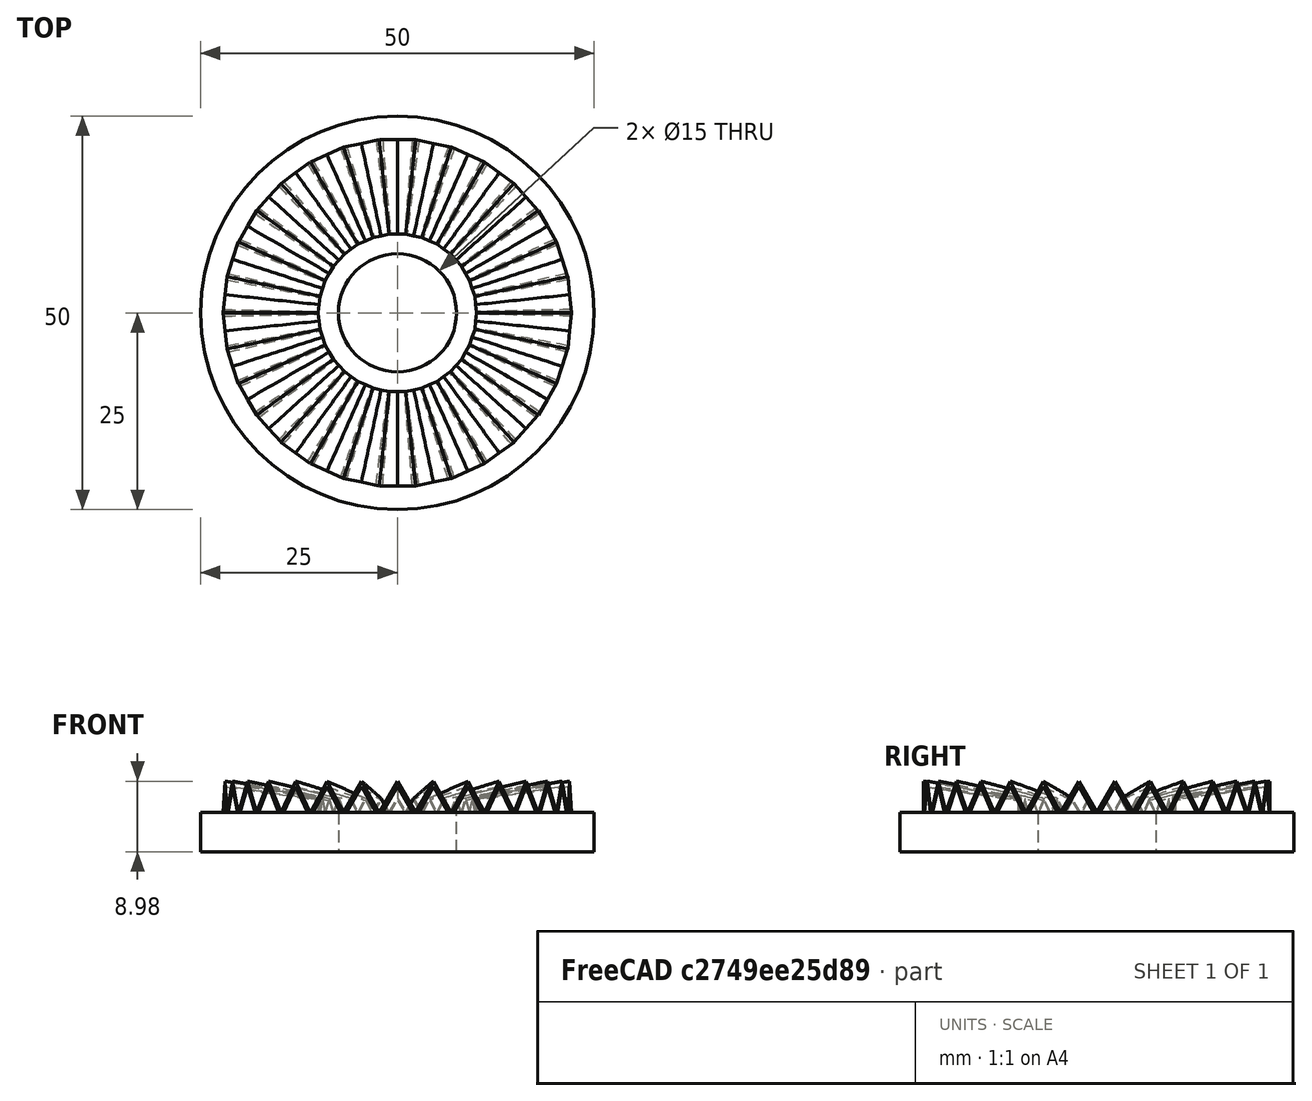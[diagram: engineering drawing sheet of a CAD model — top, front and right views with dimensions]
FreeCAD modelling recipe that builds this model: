
FCSTD DOCUMENT  (FreeCAD 1.1R20251125 (Git shallow))
Label: 20260120
License: All rights reserved
LicenseURL: http://en.wikipedia.org/wiki/All_rights_reserved
objects: Sketcher::SketchObject×8, App::Point×2, PartDesign::Pad×2, PartDesign::AdditiveLoft×2, PartDesign::PolarPattern×2, PartDesign::Body×2, Measure::MeasureDistance×2, App::DocumentObjectGroup×1, App::LinkGroup×1, App::Link×1
note: 34 computed .brp shape members not serialized (recipe doc carries the construction recipe); baked Part::Feature solids carry a one-line shape summary decoded from their .brp

FEATURE [App::Point] Origin001
  Role = Origin
FEATURE [Sketcher::SketchObject] Sketch
  ArcFitTolerance = 1e-06
  AttachmentSupport = -> [Origin]
  ExternalTypes = [0]
  FullyConstrained = true
  MakeInternals = false
  MapMode = 5
  sketch-geometry (2):
    g0: Circle CenterX=0 CenterY=0 CenterZ=0 NormalX=0 NormalY=0 NormalZ=1 AngleXU=0 Radius=25
    g1: Circle CenterX=0 CenterY=0 CenterZ=0 NormalX=0 NormalY=0 NormalZ=1 AngleXU=0 Radius=7.5
  constraints (4):
    c: Diameter(g0) = 50
    c: Coincident(g0,g-1)
    c: Diameter(g1) = 15
    c: Coincident(g0,g1)
FEATURE [PartDesign::Pad] Pad
  Direction = (0,0,1)
  Length = 5
  Length2 = 10
  Profile = -> Sketch
  ReferenceAxis = -> Sketch [N_Axis]
  Refine = true
  SideType = 0
  Suppressed = false
  Type = 0
  Type2 = 0
FEATURE [Sketcher::SketchObject] Sketch001
  ArcFitTolerance = 1e-06
  AttachmentSupport = -> [Pad]
  ExternalTypes = [0]
  FullyConstrained = true
  MakeInternals = false
  MapMode = 5
  Placement = pos=(0,0,5) rot=(0,0,1;0rad)
  sketch-geometry (6):
    g0: ArcOfCircle [constr] CenterX=0 CenterY=0 CenterZ=0 NormalX=0 NormalY=0 NormalZ=1 AngleXU=0 Radius=10 StartAngle=1.46608 EndAngle=1.67552
    g1: ArcOfCircle [constr] CenterX=0 CenterY=0 CenterZ=0 NormalX=0 NormalY=0 NormalZ=1 AngleXU=0 Radius=22 StartAngle=1.46608 EndAngle=1.67552
    g2: LineSegment [constr] StartX=0 StartY=0 StartZ=0 EndX=1.04528 EndY=9.94522 EndZ=0
    g3: LineSegment [constr] StartX=0 StartY=0 StartZ=0 EndX=-1.04528 EndY=9.94522 EndZ=0
    g4: LineSegment StartX=-1.04528 StartY=9.94522 StartZ=0 EndX=-2.29963 EndY=21.8795 EndZ=0
    g5: LineSegment StartX=2.29963 StartY=21.8795 StartZ=0 EndX=1.04528 EndY=9.94522 EndZ=0
  constraints (16):
    c: Coincident(g0,g-1)
    c: Coincident(g1,g0)
    c: Coincident(g2,g0)
    c: Coincident(g2,g0)
    c: Coincident(g3,g0)
    c: Coincident(g3,g0)
    c: Coincident(g3,g4)
    c: Coincident(g4,g1)
    c: Parallel(g4,g3)
    c: Symmetric(g1,g1,g-2)
    c: Radius(g1) = 22
    c: Radius(g0) = 10
    c: Coincident(g5,g1)
    c: Coincident(g5,g0)
    c: Parallel(g5,g2)
    c: Angle(g5,g4) = 0.20944
FEATURE [Sketcher::SketchObject] Sketch002
  ArcFitTolerance = 1e-06
  AttachmentOffset = pos=(0,0,-10) rot=(0,0,1;0rad)
  AttachmentSupport = -> [Origin]
  ExternalTypes = [0]
  FullyConstrained = true
  MakeInternals = false
  MapMode = 5
  Placement = pos=(0,10,-2.2e-15) rot=(1,0,0;1.5708rad)
  expr: Constraints[10] = href(Body.BackTooth)
  sketch-geometry (4):
    g0: LineSegment StartX=1.0455 StartY=5 StartZ=0 EndX=4e-16 EndY=6.81086 EndZ=0
    g1: LineSegment StartX=4e-16 StartY=6.81086 StartZ=0 EndX=-1.0455 EndY=5 EndZ=0
    g2: LineSegment StartX=-1.0455 StartY=5 StartZ=0 EndX=1.0455 EndY=5 EndZ=0
    g3: Circle [constr] CenterX=0 CenterY=5.60362 CenterZ=0 NormalX=0 NormalY=0 NormalZ=1 AngleXU=0 Radius=1.20724
  constraints (12):
    c: Coincident(g0,g1)
    c: Coincident(g1,g2)
    c: Coincident(g2,g0)
    c: Equal(g0,g1)
    c: Equal(g0,g2)
    c: PointOnObject(g0,g3)
    c: PointOnObject(g1,g3)
    c: PointOnObject(g2,g3)
    c: PointOnObject(g3,g-2)
    c: Horizontal(g2)
    c: Distance(g2,g2) = 2.091
    c: DistanceY(g-1,g0) = 5
FEATURE [Sketcher::SketchObject] Sketch003
  ArcFitTolerance = 1e-06
  AttachmentOffset = pos=(0,0,-22) rot=(0,0,1;0rad)
  AttachmentSupport = -> [Origin]
  ExternalTypes = [0]
  FullyConstrained = true
  MakeInternals = false
  MapMode = 5
  Placement = pos=(0,22,-4.9e-15) rot=(1,0,0;1.5708rad)
  expr: Constraints[10] = href(Body.FrontTooth)
  sketch-geometry (4):
    g0: LineSegment StartX=0 StartY=8.98285 StartZ=0 EndX=-2.2995 EndY=5 EndZ=0
    g1: LineSegment StartX=-2.2995 StartY=5 StartZ=0 EndX=2.2995 EndY=5 EndZ=0
    g2: LineSegment StartX=2.2995 StartY=5 StartZ=0 EndX=0 EndY=8.98285 EndZ=0
    g3: Circle [constr] CenterX=0 CenterY=6.32762 CenterZ=0 NormalX=0 NormalY=0 NormalZ=1 AngleXU=0 Radius=2.65523
  constraints (12):
    c: Coincident(g0,g1)
    c: Coincident(g1,g2)
    c: Coincident(g2,g0)
    c: Equal(g0,g1)
    c: Equal(g0,g2)
    c: PointOnObject(g0,g3)
    c: PointOnObject(g1,g3)
    c: PointOnObject(g2,g3)
    c: PointOnObject(g3,g-2)
    c: PointOnObject(g2,g-2)
    c: Distance(g1,g1) = 4.599
    c: DistanceY(g-1,g1) = 5
FEATURE [PartDesign::AdditiveLoft] AdditiveLoft
  BaseFeature = -> Pad
  Closed = false
  Profile = -> Sketch003
  Refine = true
  Ruled = false
  Sections = -> [Sketch002]
  Suppressed = false
FEATURE [PartDesign::PolarPattern] PolarPattern
  Angle = 360
  Axis = -> Z_Axis
  BaseFeature = -> AdditiveLoft
  Mode = 0
  Occurrences = 30
  Offset = 120
  Originals = -> [AdditiveLoft]
  Refine = true
  SpacingPattern = [0]
  Spacings = [-1,-1,-1,-1,-1,-1,-1,-1,-1,-1,-1,-1,-1,-1,-1,-1,-1,-1,-1,-1,-1,-1,-1,-1,-1,-1,-1,-1,-1]
  Suppressed = false
  TransformMode = 0
FEATURE [PartDesign::Body] Body
  AllowCompound = true
  BackTooth = 2.091
  FrontTooth = 4.599
  Group = -> [Sketch,Pad,Sketch001,Sketch002,Sketch003,AdditiveLoft,PolarPattern]
  Origin = -> Origin
  Tip = -> PolarPattern
FEATURE [Measure::MeasureDistance] Distance  label="Distance: 2,091 mm"
  Distance = 2.09057
  DistanceX = 2.09057
  DistanceY = 0
  DistanceZ = 0
  Element1 = -> Body [Sketch001.Vertex1]
  Element2 = -> Body [Sketch001.Vertex4]
  Position1 = (-1.04528,9.94522,5)
  Position2 = (1.04528,9.94522,5)
FEATURE [Measure::MeasureDistance] Distance001  label="Distance001: 4,599 mm"
  Distance = 4.59925
  DistanceX = 4.59925
  DistanceY = 0
  DistanceZ = 0
  Element1 = -> Body [Sketch001.Vertex2]
  Element2 = -> Body [Sketch001.Vertex3]
  Position1 = (-2.29963,21.8795,5)
  Position2 = (2.29963,21.8795,5)
FEATURE [App::DocumentObjectGroup] Measurements
  Group = -> [Distance,Distance001]
FEATURE [App::Point] Origin002
  Role = Origin
FEATURE [Sketcher::SketchObject] Sketch004
  ArcFitTolerance = 1e-06
  AttachmentOffset = pos=(0,0,-10) rot=(0,0,1;0rad)
  AttachmentSupport = -> [Origin003]
  ExternalTypes = [0]
  FullyConstrained = true
  MakeInternals = false
  MapMode = 5
  Placement = pos=(0,10,-2.2e-15) rot=(1,0,0;1.5708rad)
  expr: Constraints[10] = href(Body001.BackTooth)
  sketch-geometry (4):
    g0: LineSegment StartX=0.8955 StartY=5 StartZ=0 EndX=0 EndY=6.55105 EndZ=0
    g1: LineSegment StartX=0 StartY=6.55105 StartZ=0 EndX=-0.8955 EndY=5 EndZ=0
    g2: LineSegment StartX=-0.8955 StartY=5 StartZ=0 EndX=0.8955 EndY=5 EndZ=0
    g3: Circle [constr] CenterX=0 CenterY=5.51702 CenterZ=0 NormalX=0 NormalY=0 NormalZ=1 AngleXU=0 Radius=1.03403
  constraints (12):
    c: Coincident(g0,g1)
    c: Coincident(g1,g2)
    c: Coincident(g2,g0)
    c: Equal(g0,g1)
    c: Equal(g0,g2)
    c: PointOnObject(g0,g3)
    c: PointOnObject(g1,g3)
    c: PointOnObject(g2,g3)
    c: PointOnObject(g3,g-2)
    c: Horizontal(g2)
    c: Distance(g2,g2) = 1.791
    c: DistanceY(g-1,g0) = 5
FEATURE [Sketcher::SketchObject] Sketch005
  ArcFitTolerance = 1e-06
  AttachmentOffset = pos=(0,0,-22) rot=(0,0,1;0rad)
  AttachmentSupport = -> [Origin003]
  ExternalTypes = [0]
  FullyConstrained = true
  MakeInternals = false
  MapMode = 5
  Placement = pos=(0,22,-4.9e-15) rot=(1,0,0;1.5708rad)
  expr: Constraints[10] = href(Body001.FrontTooth)
  sketch-geometry (4):
    g0: LineSegment StartX=0 StartY=8.29003 StartZ=0 EndX=-1.8995 EndY=5 EndZ=0
    g1: LineSegment StartX=-1.8995 StartY=5 StartZ=0 EndX=1.8995 EndY=5 EndZ=0
    g2: LineSegment StartX=1.8995 StartY=5 StartZ=0 EndX=0 EndY=8.29003 EndZ=0
    g3: Circle [constr] CenterX=0 CenterY=6.09668 CenterZ=0 NormalX=0 NormalY=0 NormalZ=1 AngleXU=0 Radius=2.19335
  constraints (12):
    c: Coincident(g0,g1)
    c: Coincident(g1,g2)
    c: Coincident(g2,g0)
    c: Equal(g0,g1)
    c: Equal(g0,g2)
    c: PointOnObject(g0,g3)
    c: PointOnObject(g1,g3)
    c: PointOnObject(g2,g3)
    c: PointOnObject(g3,g-2)
    c: PointOnObject(g2,g-2)
    c: Distance(g1,g1) = 3.799
    c: DistanceY(g-1,g1) = 5
FEATURE [Sketcher::SketchObject] Sketch006
  ArcFitTolerance = 1e-06
  AttachmentSupport = -> [Origin003]
  ExternalTypes = [0]
  FullyConstrained = true
  MakeInternals = false
  MapMode = 5
  sketch-geometry (2):
    g0: Circle CenterX=0 CenterY=0 CenterZ=0 NormalX=0 NormalY=0 NormalZ=1 AngleXU=0 Radius=25
    g1: Circle CenterX=0 CenterY=0 CenterZ=0 NormalX=0 NormalY=0 NormalZ=1 AngleXU=0 Radius=7.5
  constraints (4):
    c: Diameter(g0) = 50
    c: Coincident(g0,g-1)
    c: Diameter(g1) = 15
    c: Coincident(g0,g1)
FEATURE [PartDesign::Pad] Pad001
  Direction = (0,0,1)
  Length = 5
  Length2 = 10
  Profile = -> Sketch006
  ReferenceAxis = -> Sketch006 [N_Axis]
  Refine = true
  SideType = 0
  Suppressed = false
  Type = 0
  Type2 = 0
FEATURE [PartDesign::AdditiveLoft] AdditiveLoft001
  BaseFeature = -> Pad001
  Closed = false
  Profile = -> Sketch005
  Refine = true
  Ruled = false
  Sections = -> [Sketch004]
  Suppressed = false
FEATURE [PartDesign::PolarPattern] PolarPattern001
  Angle = 360
  Axis = -> Z_Axis001
  BaseFeature = -> AdditiveLoft001
  Mode = 0
  Occurrences = 30
  Offset = 120
  Originals = -> [AdditiveLoft001]
  Refine = true
  SpacingPattern = [0]
  Spacings = [-1,-1,-1,-1,-1,-1,-1,-1,-1,-1,-1,-1,-1,-1,-1,-1,-1,-1,-1,-1,-1,-1,-1,-1,-1,-1,-1,-1,-1]
  Suppressed = false
  TransformMode = 0
FEATURE [Sketcher::SketchObject] Sketch007
  ArcFitTolerance = 1e-06
  AttachmentSupport = -> [Pad001]
  ExternalTypes = [0]
  FullyConstrained = true
  MakeInternals = false
  MapMode = 5
  Placement = pos=(0,0,5) rot=(0,0,1;0rad)
  sketch-geometry (6):
    g0: ArcOfCircle [constr] CenterX=0 CenterY=0 CenterZ=0 NormalX=0 NormalY=0 NormalZ=1 AngleXU=0 Radius=10 StartAngle=1.46608 EndAngle=1.67552
    g1: ArcOfCircle [constr] CenterX=0 CenterY=0 CenterZ=0 NormalX=0 NormalY=0 NormalZ=1 AngleXU=0 Radius=22 StartAngle=1.46608 EndAngle=1.67552
    g2: LineSegment [constr] StartX=0 StartY=0 StartZ=0 EndX=1.04528 EndY=9.94522 EndZ=0
    g3: LineSegment [constr] StartX=0 StartY=0 StartZ=0 EndX=-1.04528 EndY=9.94522 EndZ=0
    g4: LineSegment StartX=-1.04528 StartY=9.94522 StartZ=0 EndX=-2.29963 EndY=21.8795 EndZ=0
    g5: LineSegment StartX=2.29963 StartY=21.8795 StartZ=0 EndX=1.04528 EndY=9.94522 EndZ=0
  constraints (16):
    c: Coincident(g0,g-1)
    c: Coincident(g1,g0)
    c: Coincident(g2,g0)
    c: Coincident(g2,g0)
    c: Coincident(g3,g0)
    c: Coincident(g3,g0)
    c: Coincident(g3,g4)
    c: Coincident(g4,g1)
    c: Parallel(g4,g3)
    c: Symmetric(g1,g1,g-2)
    c: Radius(g1) = 22
    c: Radius(g0) = 10
    c: Coincident(g5,g1)
    c: Coincident(g5,g0)
    c: Parallel(g5,g2)
    c: Angle(g5,g4) = 0.20944
FEATURE [PartDesign::Body] Body001  label="Body002"
  AllowCompound = true
  BackTooth = 1.791
  FrontTooth = 3.799
  Group = -> [Sketch006,Pad001,Sketch007,Sketch004,Sketch005,AdditiveLoft001,PolarPattern001]
  Origin = -> Origin003
  Tip = -> PolarPattern001
FEATURE [App::LinkGroup] CopyOnChangeGroup
  ElementList = -> [Body001,Sketch007,PolarPattern001,AdditiveLoft001,Pad001,Sketch006,Sketch005,Sketch004,Origin003,Origin002,YZ_Plane001,XZ_Plane001,XY_Plane001,Y_Axis001,X_Axis001,Z_Axis001]
  LinkMode = 1
FEATURE [App::Link] Link  label="Body001"
  BackTooth = 1.791
  FrontTooth = 3.799
  LinkCopyOnChange = 2
  LinkCopyOnChangeGroup = -> CopyOnChangeGroup
  LinkCopyOnChangeSource = -> Body
  LinkCopyOnChangeTouched = true
  LinkPlacement = pos=(0,0,13.4) rot=(0.99863,0.052336,0;3.14159rad)
  LinkedObject = -> Body001
  Placement = pos=(0,0,13.4) rot=(0.99863,0.052336,0;3.14159rad)
